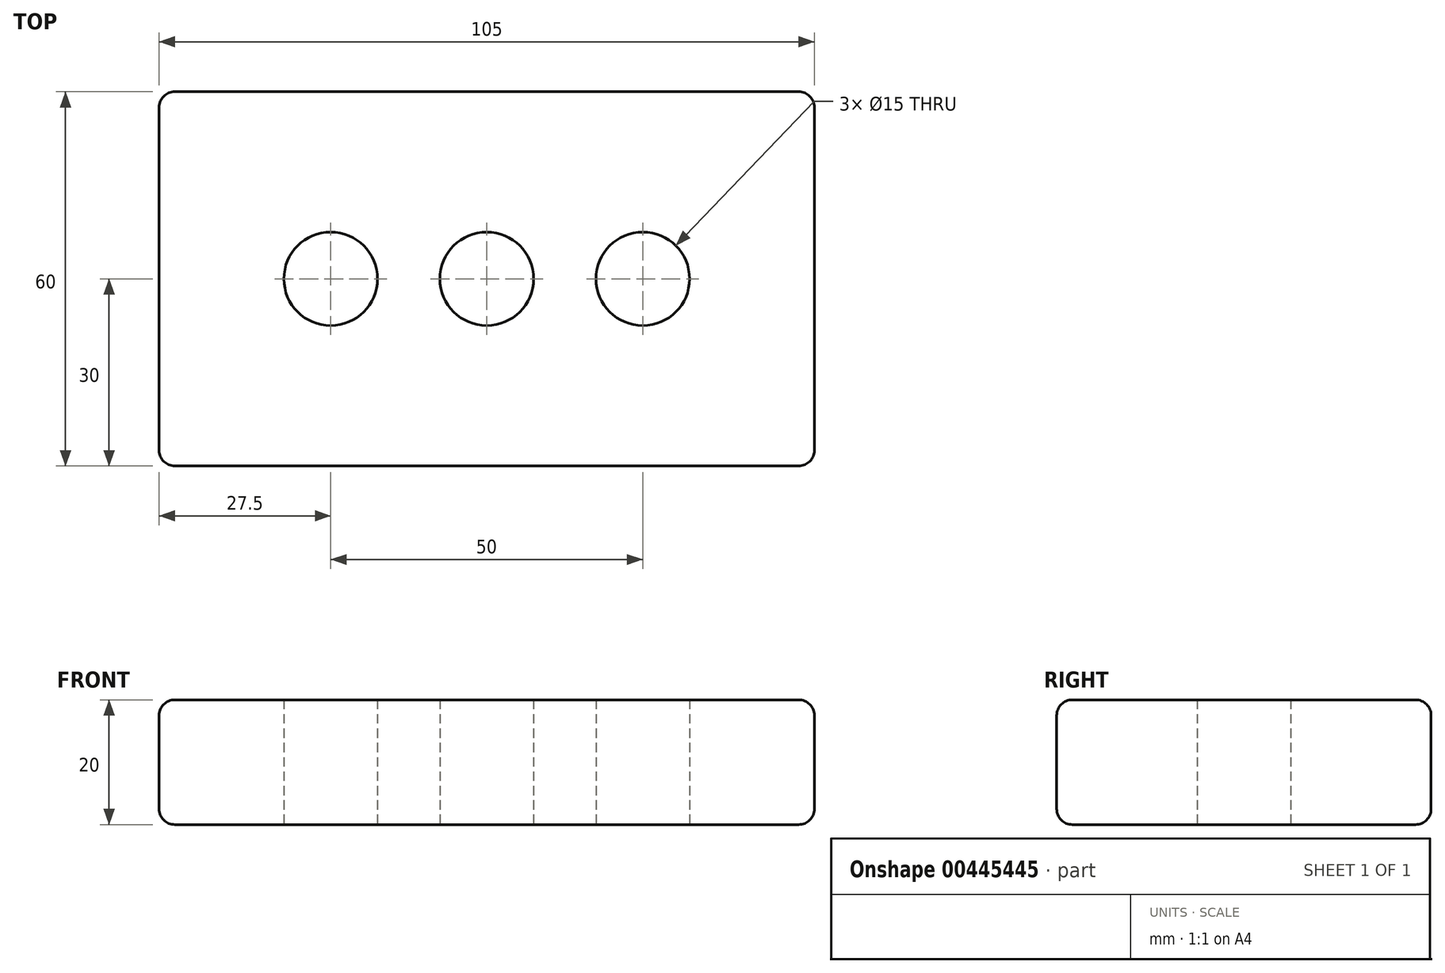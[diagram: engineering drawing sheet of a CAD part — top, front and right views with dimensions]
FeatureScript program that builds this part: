
annotation { "Feature Type Name" : "Feature", "Feature Type Description" : "" }
export const myFeature = defineFeature(function(context is Context, id is Id, definition is map)
    precondition{}
    {
        {
            var Q0;
            Q0=qCreatedBy(makeId("Top.planeOp"),FACE);
            var sketch = newSketch(context, id + "F0", { "sketchPlane" : qUnion([Q0])});
            skLineSegment(sketch, "E0.bottom", {"start": v(52.5, -30) * mm, "end": v(-52.5, -30) * mm});
            skLineSegment(sketch, "E0.top", {"start": v(52.5, 30) * mm, "end": v(-52.5, 30) * mm});
            skLineSegment(sketch, "E0.left", {"start": v(52.5, -30) * mm, "end": v(52.5, 30) * mm});
            skLineSegment(sketch, "E0.right", {"start": v(-52.5, -30) * mm, "end": v(-52.5, 30) * mm});
            skPoint(sketch, "E0.middle", {"position": v(0, 0) * mm});
            skCircle(sketch, "E1", {"center": v(0, 0) * mm, "radius": 7.5 * mm});
            skLineSegment(sketch, "E2", {"start": v(0, 0) * mm, "end": v(25, 0) * mm});
            skCircle(sketch, "E3", {"center": v(25, 0) * mm, "radius": 7.5 * mm});
            skLineSegment(sketch, "E4", {"start": v(0, 0) * mm, "end": v(-25, 0) * mm});
            skCircle(sketch, "E5", {"center": v(-25, 0) * mm, "radius": 7.5 * mm});
            skSolve(sketch);
        }
        {
            var Q0;
            Q0 = qSketchRegion(id + "F0", true);
            extrude(context, id + "F1", {"entities" : qUnion([Q0]), "depth" : 20 * mm});
        }
        {
            var Q0;
            Q0=makeQuery(id+"F1.opExtrude","CAP_EDGE",EDGE,{"disambiguationData":[OSD([sQuery(id+"F0.wireOp",EDGE,"E0.top")])],"isStart":false});
            var Q1;
            Q1=makeQuery(id+"F1.opExtrude","SWEPT_EDGE",EDGE,{"disambiguationData":[OSD([sQuery(id+"F0.wireOp",EDGE,"E0.top"),sQuery(id+"F0.wireOp",EDGE,"E0.right")])]});
            var Q2;
            Q2=makeQuery(id+"F1.opExtrude","CAP_EDGE",EDGE,{"disambiguationData":[OSD([sQuery(id+"F0.wireOp",EDGE,"E0.top")])],"isStart":true});
            var Q3;
            Q3=makeQuery(id+"F1.opExtrude","SWEPT_EDGE",EDGE,{"disambiguationData":[OSD([sQuery(id+"F0.wireOp",EDGE,"E0.top"),sQuery(id+"F0.wireOp",EDGE,"E0.left")])]});
            var Q4;
            Q4=makeQuery(id+"F1.opExtrude","CAP_EDGE",EDGE,{"disambiguationData":[OSD([sQuery(id+"F0.wireOp",EDGE,"E0.bottom")])],"isStart":true});
            var Q5;
            Q5=makeQuery(id+"F1.opExtrude","CAP_EDGE",EDGE,{"disambiguationData":[OSD([sQuery(id+"F0.wireOp",EDGE,"E0.right")])],"isStart":true});
            var Q6;
            Q6=makeQuery(id+"F1.opExtrude","CAP_EDGE",EDGE,{"disambiguationData":[OSD([sQuery(id+"F0.wireOp",EDGE,"E0.left")])],"isStart":true});
            var Q7;
            Q7=makeQuery(id+"F1.opExtrude","SWEPT_EDGE",EDGE,{"disambiguationData":[OSD([sQuery(id+"F0.wireOp",EDGE,"E0.bottom"),sQuery(id+"F0.wireOp",EDGE,"E0.right")])]});
            var Q8;
            Q8=makeQuery(id+"F1.opExtrude","CAP_EDGE",EDGE,{"disambiguationData":[OSD([sQuery(id+"F0.wireOp",EDGE,"E0.bottom")])],"isStart":false});
            var Q9;
            Q9=makeQuery(id+"F1.opExtrude","SWEPT_EDGE",EDGE,{"disambiguationData":[OSD([sQuery(id+"F0.wireOp",EDGE,"E0.bottom"),sQuery(id+"F0.wireOp",EDGE,"E0.left")])]});
            var Q10;
            Q10=makeQuery(id+"F1.opExtrude","CAP_EDGE",EDGE,{"disambiguationData":[OSD([sQuery(id+"F0.wireOp",EDGE,"E0.right")])],"isStart":false});
            var Q11;
            Q11=makeQuery(id+"F1.opExtrude","CAP_EDGE",EDGE,{"disambiguationData":[OSD([sQuery(id+"F0.wireOp",EDGE,"E0.left")])],"isStart":false});
            fillet(context, id + "F2", {"entities" : qUnion([Q0, Q1, Q2, Q3, Q4, Q5, Q6, Q7, Q8, Q9, Q10, Q11]), "radius" : 2.5 * mm, "tangentPropagation" : true, "allowEdgeOverflow" : false});
        }
    });
